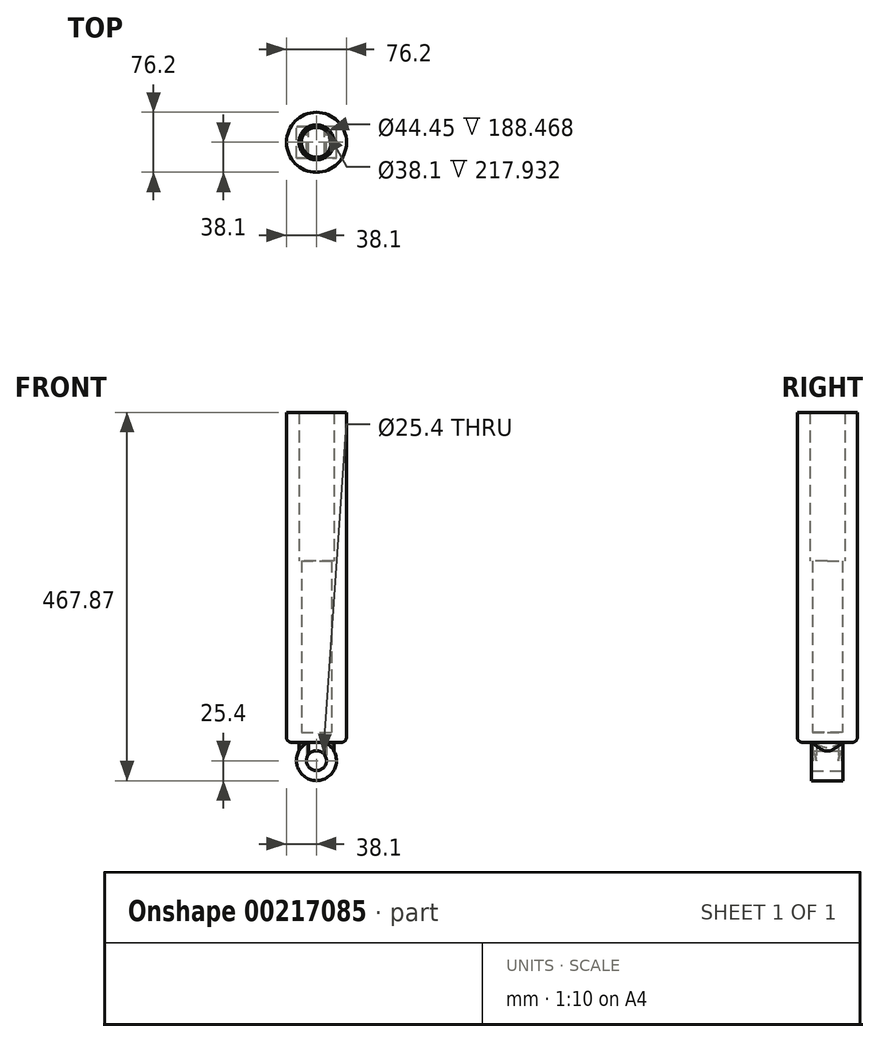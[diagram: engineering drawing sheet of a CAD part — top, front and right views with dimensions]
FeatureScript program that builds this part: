
annotation { "Feature Type Name" : "Feature", "Feature Type Description" : "" }
export const myFeature = defineFeature(function(context is Context, id is Id, definition is map)
    precondition{}
    {
        {
            var Q0;
            Q0=qCreatedBy(makeId("Front.planeOp"),FACE);
            var sketch = newSketch(context, id + "F0", { "sketchPlane" : qUnion([Q0])});
            skCircle(sketch, "E0", {"center": v(0, 0) * mm, "radius": 12.7 * mm});
            skCircle(sketch, "E1", {"center": v(0, 0) * mm, "radius": 25.4 * mm});
            skSolve(sketch);
        }
        {
            var Q0;
            Q0=qCreatedBy(makeId("Top.planeOp"),FACE);
            var sketch = newSketch(context, id + "F1", { "sketchPlane" : qUnion([Q0])});
            skCircle(sketch, "E2", {"center": v(0, 0) * mm, "radius": 19.05 * mm});
            skCircle(sketch, "E3", {"center": v(0, 0) * mm, "radius": 22.23 * mm});
            skSolve(sketch);
        }
        {
            var Q0;
            Q0=makeQuery(id+"F0.imprint","IMPRINT",FACE,{"disambiguationData":[TD([[makeQuery(id+"F0.imprint","IMPRINT",EDGE,{"derivedFrom":sQuery(id+"F0.wireOp",EDGE,"E0")}),-1.0]])]});
            extrude(context, id + "F2", {"entities" : qUnion([Q0]), "depth" : 39.88 * mm, "symmetric" : true});
        }
        {
            var Q0;
            Q0=makeQuery(id+"F1.imprint","IMPRINT",FACE,{"disambiguationData":[TD([[makeQuery(id+"F1.imprint","IMPRINT",EDGE,{"derivedFrom":sQuery(id+"F1.wireOp",EDGE,"E2")}),-1.0]])]});
            extrude(context, id + "F3", {"entities" : qUnion([Q0]), "operationType" : NewBodyOperationType.ADD, "depth" : 254 * mm});
        }
        {
            var Q0;
            Q0=makeQuery(id+"F3.boolean.opBoolean","SPLIT",FACE,{"disambiguationData":[OD(0.0)],"derivedFrom":makeQuery(id+"F3.opExtrude","CAP_FACE",FACE,{"disambiguationData":[OSD([sQuery(id+"F1.wireOp",EDGE,"E2"),sQuery(id+"F1.wireOp",EDGE,"E3")])],"isStart":true})});
            var Q1;
            Q1=makeQuery(id+"F3.boolean.opBoolean","SPLIT",FACE,{"disambiguationData":[OD(1.0)],"derivedFrom":makeQuery(id+"F3.opExtrude","CAP_FACE",FACE,{"disambiguationData":[OSD([sQuery(id+"F1.wireOp",EDGE,"E2"),sQuery(id+"F1.wireOp",EDGE,"E3")])],"isStart":true})});
            extrude(context, id + "F4", {"entities" : qUnion([Q0, Q1]), "operationType" : NewBodyOperationType.REMOVE, "oppositeDirection" : true, "depth" : 29.72 * mm});
        }
        {
            var Q0;
            {var subQ0=sQuery(id+"F1.wireOp",EDGE,"E3");var subQ1=sQuery(id+"F1.wireOp",EDGE,"E2");Q0=makeQuery(id+"F4.boolean.opBoolean","COPY",FACE,{"derivedFrom":makeQuery(id+"F4.opExtrude","CAP_FACE",FACE,{"disambiguationData":[OSD([subQ1,subQ0]),TDD([makeQuery(id+"F3.boolean.opBoolean","SPLIT",FACE,{"disambiguationData":[OD(1.0)],"derivedFrom":makeQuery(id+"F3.opExtrude","CAP_FACE",FACE,{"disambiguationData":[OSD([subQ1,subQ0])],"isStart":true})})])],"isStart":false})});}
            var sketch = newSketch(context, id + "F5", { "sketchPlane" : qUnion([Q0])});
            skCircle(sketch, "E4", {"center": v(0, 0) * mm, "radius": 38.1 * mm});
            skSolve(sketch);
        }
        {
            var Q0;
            Q0 = qSketchRegion(id + "F5", true);
            extrude(context, id + "F6", {"entities" : qUnion([Q0]), "operationType" : NewBodyOperationType.ADD, "depth" : 12.7 * mm, "symmetric" : true});
        }
        {
            var Q0;
            {var subQ0=sQuery(id+"F5.wireOp",EDGE,"E4");Q0=makeQuery(id+"F6.boolean.opBoolean","SPLIT",FACE,{"disambiguationData":[TD([makeQuery(id+"F3.opExtrude","SWEPT_FACE",FACE,{"disambiguationData":[OSD([sQuery(id+"F1.wireOp",EDGE,"E3")])]})])],"derivedFrom":makeQuery(id+"F6.opExtrude","CAP_FACE",FACE,{"disambiguationData":[OSD([subQ0])],"isStart":true})});}
            extrude(context, id + "F7", {"entities" : qUnion([Q0]), "operationType" : NewBodyOperationType.ADD, "depth" : 406.4 * mm});
        }
        {
            var Q0;
            Q0=makeQuery(id+"F6.opExtrude","CAP_EDGE",EDGE,{"disambiguationData":[OSD([sQuery(id+"F5.wireOp",EDGE,"E4")])],"isStart":false});
            fillet(context, id + "F8", {"entities" : qUnion([Q0]), "radius" : 6.35 * mm, "tangentPropagation" : true, "allowEdgeOverflow" : false});
        }
    });
